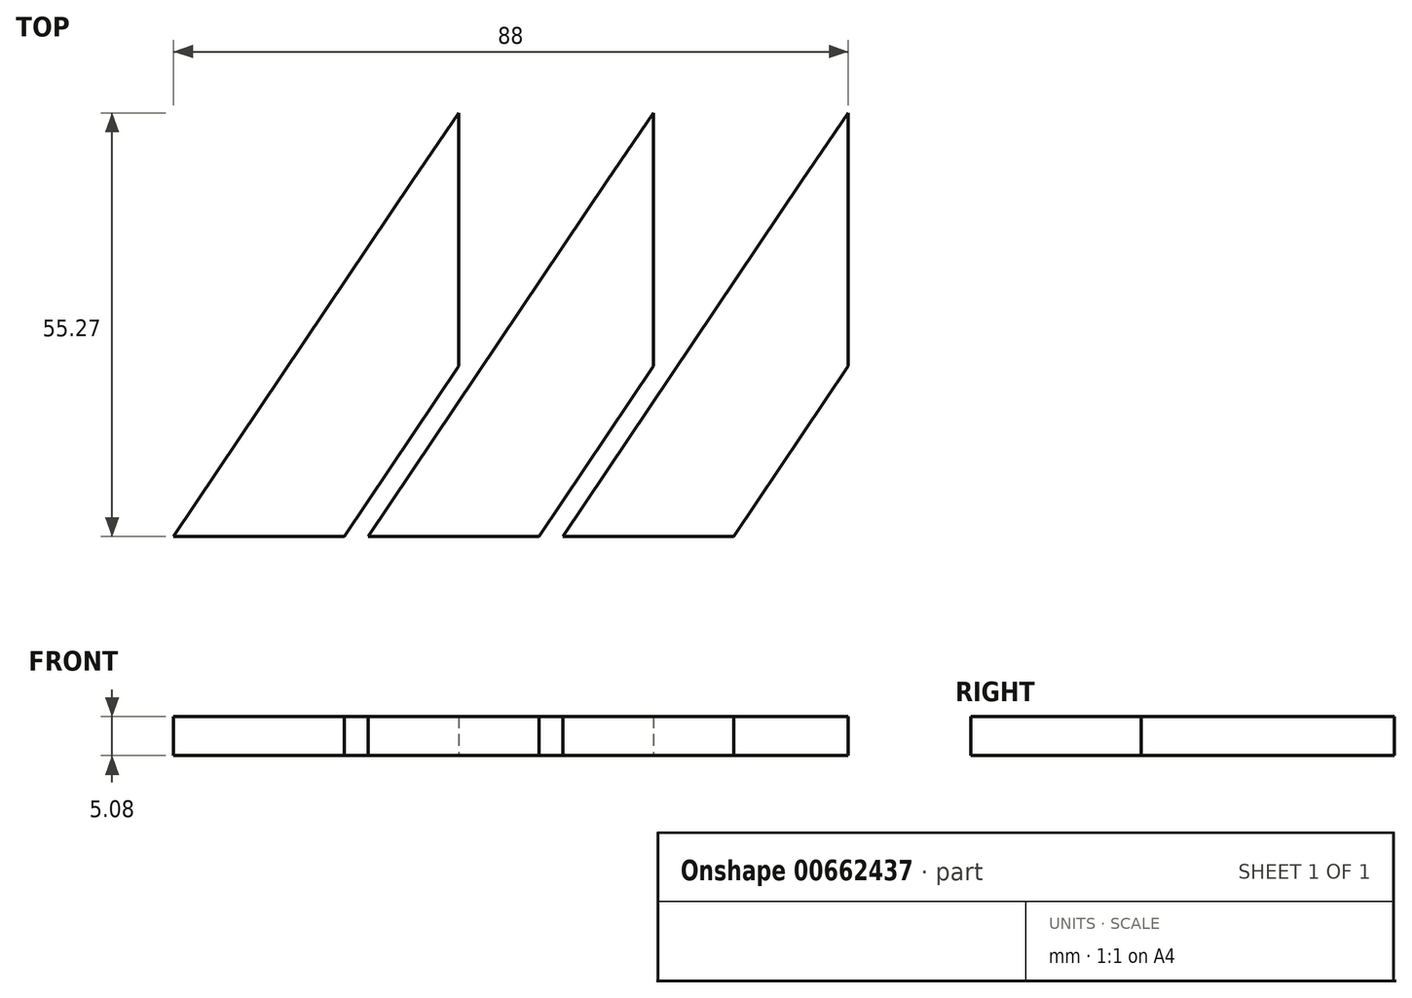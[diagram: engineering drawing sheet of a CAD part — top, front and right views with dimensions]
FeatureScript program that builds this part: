
annotation { "Feature Type Name" : "Feature", "Feature Type Description" : "" }
export const myFeature = defineFeature(function(context is Context, id is Id, definition is map)
    precondition{}
    {
        {
            var Q0;
            Q0=qCreatedBy(makeId("Top.planeOp"),FACE);
            var sketch = newSketch(context, id + "F0", { "sketchPlane" : qUnion([Q0])});
            skLineSegment(sketch, "E0", {"start": v(-35.27, 57.56) * mm, "end": v(-66.42, 11.15) * mm});
            skLineSegment(sketch, "E1", {"start": v(-66.42, 11.15) * mm, "end": v(-44.13, 11.15) * mm});
            skLineSegment(sketch, "E2", {"start": v(-44.13, 11.15) * mm, "end": v(-29.22, 33.37) * mm});
            skLineSegment(sketch, "E3", {"start": v(-29.22, 33.37) * mm, "end": v(-29.22, 66.42) * mm});
            skLineSegment(sketch, "E4", {"start": v(-35.27, 57.56) * mm, "end": v(-29.22, 66.42) * mm});
            skLineSegment(sketch, "E5.1.0.0", {"start": v(-3.82, 33.37) * mm, "end": v(-3.82, 66.42) * mm});
            skLineSegment(sketch, "E5.1.0.1", {"start": v(-18.73, 11.15) * mm, "end": v(-3.82, 33.37) * mm});
            skLineSegment(sketch, "E5.1.0.2", {"start": v(-41.02, 11.15) * mm, "end": v(-18.73, 11.15) * mm});
            skLineSegment(sketch, "E5.2.0.0", {"start": v(21.58, 33.37) * mm, "end": v(21.58, 66.42) * mm});
            skLineSegment(sketch, "E5.2.0.1", {"start": v(6.67, 11.15) * mm, "end": v(21.58, 33.37) * mm});
            skLineSegment(sketch, "E5.2.0.2", {"start": v(-15.62, 11.15) * mm, "end": v(6.67, 11.15) * mm});
            skLineSegment(sketch, "E5.direction1", {"start": v(-29.22, 33.37) * mm, "end": v(-3.82, 33.37) * mm, "construction": true});
            skLineSegment(sketch, "E6.1.0.0", {"start": v(-9.87, 57.56) * mm, "end": v(-41.02, 11.15) * mm});
            skLineSegment(sketch, "E6.1.0.1", {"start": v(-9.87, 57.56) * mm, "end": v(-3.82, 66.42) * mm});
            skLineSegment(sketch, "E6.2.0.0", {"start": v(15.53, 57.56) * mm, "end": v(-15.62, 11.15) * mm});
            skLineSegment(sketch, "E6.2.0.1", {"start": v(15.53, 57.56) * mm, "end": v(21.58, 66.42) * mm});
            skLineSegment(sketch, "E6.direction1", {"start": v(-66.42, 11.15) * mm, "end": v(-41.02, 11.15) * mm, "construction": true});
            skSolve(sketch);
        }
        {
            var Q0;
            Q0=makeQuery(id+"F0.imprint","IMPRINT",FACE,{"disambiguationData":[TD([[makeQuery(id+"F0.imprint","IMPRINT",EDGE,{"derivedFrom":sQuery(id+"F0.wireOp",EDGE,"E5.1.0.0")}),1.0]])]});
            var Q1;
            Q1=makeQuery(id+"F0.imprint","IMPRINT",FACE,{"disambiguationData":[TD([[makeQuery(id+"F0.imprint","IMPRINT",EDGE,{"derivedFrom":sQuery(id+"F0.wireOp",EDGE,"E5.2.0.0")}),1.0]])]});
            var Q2;
            Q2=makeQuery(id+"F0.imprint","IMPRINT",FACE,{"disambiguationData":[TD([[makeQuery(id+"F0.imprint","IMPRINT",EDGE,{"derivedFrom":sQuery(id+"F0.wireOp",EDGE,"E0")}),1.0]])]});
            extrude(context, id + "F1", {"entities" : qUnion([Q0, Q1, Q2]), "depth" : 5.08 * mm, "offsetDistance" : 25.4 * mm});
        }
    });
